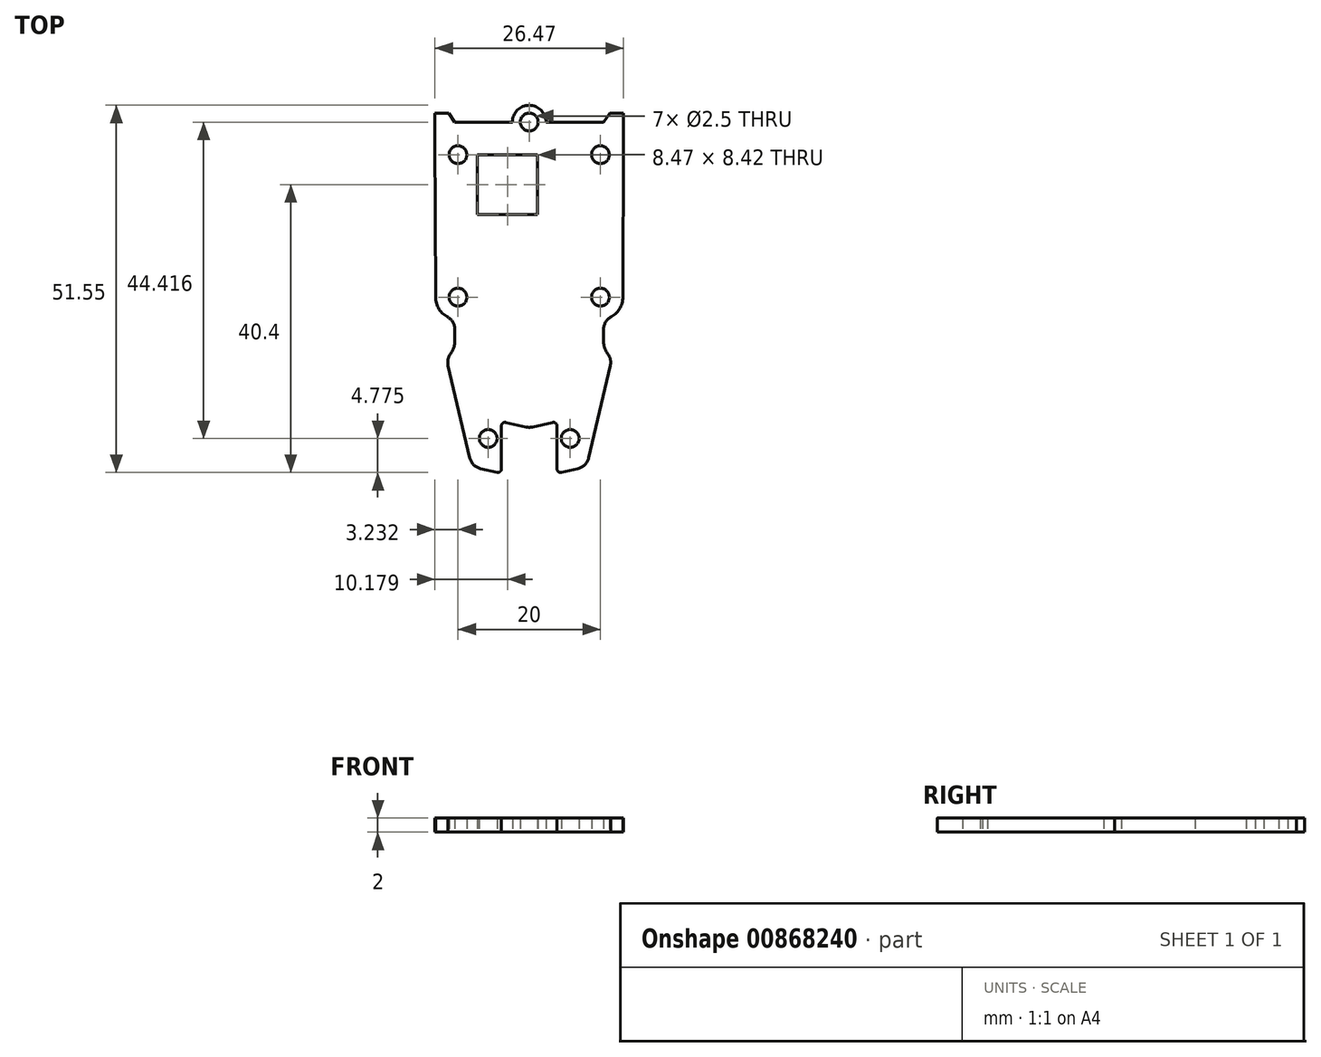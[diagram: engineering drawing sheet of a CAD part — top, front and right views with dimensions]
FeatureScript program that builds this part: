
annotation { "Feature Type Name" : "Feature", "Feature Type Description" : "" }
export const myFeature = defineFeature(function(context is Context, id is Id, definition is map)
    precondition{}
    {
        {
            var Q0;
            Q0=qCreatedBy(makeId("Top.planeOp"),FACE);
            var sketch = newSketch(context, id + "F0", { "sketchPlane" : qUnion([Q0])});
            skLineSegment(sketch, "E0.bottom", {"start": v(31.73, 23.79) * mm, "end": v(11.73, 23.79) * mm, "construction": true});
            skLineSegment(sketch, "E0.top", {"start": v(31.73, 43.79) * mm, "end": v(11.73, 43.79) * mm, "construction": true});
            skLineSegment(sketch, "E0.right", {"start": v(11.73, 23.79) * mm, "end": v(11.73, 43.79) * mm, "construction": true});
            skPoint(sketch, "E0.middle", {"position": v(21.73, 33.79) * mm});
            skCircle(sketch, "E1", {"center": v(11.73, 43.79) * mm, "radius": 1.25 * mm});
            skCircle(sketch, "E2.MirrorC", {"center": v(11.73, 23.79) * mm, "radius": 1.25 * mm});
            skLineSegment(sketch, "E3", {"start": v(12.51, 48.37) * mm, "end": v(19.38, 48.37) * mm});
            skLineSegment(sketch, "E4.MirrorCS", {"start": v(30.95, 48.37) * mm, "end": v(24.09, 48.37) * mm});
            skArc(sketch, "E5.0", {"start": v(10.25, 21.01) * mm, "mid": v(8.96, 22.28) * mm, "end": v(8.6, 24.05) * mm});
            skLineSegment(sketch, "E6", {"start": v(11.3, 17.66) * mm, "end": v(11.3, 19.25) * mm});
            skPoint(sketch, "E7.visualSharp", {"position": v(8.68, 24.79) * mm});
            skPoint(sketch, "E8.visualSharp", {"position": v(11.59, 20.92) * mm});
            skArc(sketch, "E8.filletArc", {"start": v(11.3, 19.25) * mm, "mid": v(11.02, 20.28) * mm, "end": v(10.25, 21.01) * mm});
            skPoint(sketch, "E9.orphan", {"position": v(11.3, 13.07) * mm});
            skArc(sketch, "E10.MirrorCS", {"start": v(33.8, 46.17) * mm, "mid": v(33.8, 46.16) * mm, "end": v(33.8, 46.16) * mm});
            skArc(sketch, "E11.MirrorCS", {"start": v(33.22, 21.01) * mm, "mid": v(34.5, 22.28) * mm, "end": v(34.87, 24.05) * mm});
            skArc(sketch, "E12.MirrorCS", {"start": v(32.16, 19.25) * mm, "mid": v(32.45, 20.28) * mm, "end": v(33.22, 21.01) * mm});
            skLineSegment(sketch, "E13.MirrorCS", {"start": v(32.16, 17.66) * mm, "end": v(32.16, 19.25) * mm});
            skCircle(sketch, "E14.MirrorC", {"center": v(31.73, 23.79) * mm, "radius": 1.25 * mm});
            skPoint(sketch, "E15.MirrorP", {"position": v(32.16, 20.67) * mm});
            skCircle(sketch, "E16.MirrorC", {"center": v(31.73, 43.79) * mm, "radius": 1.25 * mm});
            skPoint(sketch, "E17.MirrorP", {"position": v(32.16, 13.07) * mm});
            skLineSegment(sketch, "E18.MirrorCS", {"start": v(31.73, 23.79) * mm, "end": v(31.73, 43.79) * mm, "construction": true});
            skLineSegment(sketch, "E19", {"start": v(11.28, 48.36) * mm, "end": v(12.51, 48.37) * mm});
            skLineSegment(sketch, "E20.MirrorCS", {"start": v(32.18, 48.36) * mm, "end": v(30.95, 48.37) * mm});
            skPoint(sketch, "E21.MirrorCS.end.orphan", {"position": v(30.95, 48.37) * mm});
            skArc(sketch, "E22", {"start": v(24.09, 48.37) * mm, "mid": v(21.73, 50.73) * mm, "end": v(19.38, 48.37) * mm});
            skCircle(sketch, "E23", {"center": v(21.73, 48.37) * mm, "radius": 1.25 * mm});
            skCircle(sketch, "E24", {"center": v(15.98, 3.96) * mm, "radius": 1.25 * mm});
            skCircle(sketch, "E25.MirrorC", {"center": v(27.48, 3.96) * mm, "radius": 1.25 * mm});
            skPoint(sketch, "E26.visualSharp", {"position": v(11.3, 16.16) * mm});
            skArc(sketch, "E26.filletArc", {"start": v(10.7, 15.85) * mm, "mid": v(11.15, 16.7) * mm, "end": v(11.3, 17.66) * mm});
            skPoint(sketch, "E27.visualSharp", {"position": v(32.16, 16.16) * mm});
            skArc(sketch, "E27.filletArc", {"start": v(32.16, 17.66) * mm, "mid": v(32.32, 16.7) * mm, "end": v(32.76, 15.85) * mm});
            skPoint(sketch, "E28.MirrorP", {"position": v(33.1, 46.2) * mm});
            skPoint(sketch, "E29.visualSharp", {"position": v(29.24, 0.28) * mm});
            skLineSegment(sketch, "E30.MirrorCS", {"start": v(28.57, -0.28) * mm, "end": v(26.24, -0.8) * mm});
            skLineSegment(sketch, "E31", {"start": v(10.35, 14.2) * mm, "end": v(13.39, 1.22) * mm});
            skLineSegment(sketch, "E32", {"start": v(33.11, 14.2) * mm, "end": v(30.08, 1.22) * mm});
            skLineSegment(sketch, "E33", {"start": v(17.83, -0.32) * mm, "end": v(17.83, 5.72) * mm});
            skLineSegment(sketch, "E34", {"start": v(18.45, 6.2) * mm, "end": v(21.29, 5.56) * mm});
            skLineSegment(sketch, "E35", {"start": v(21.73, 5.46) * mm, "end": v(21.73, -1.74) * mm, "construction": true});
            skLineSegment(sketch, "E36.MirrorCS", {"start": v(25.02, 6.2) * mm, "end": v(22.17, 5.56) * mm});
            skLineSegment(sketch, "E37.MirrorCS", {"start": v(25.63, -0.32) * mm, "end": v(25.63, 5.72) * mm});
            skPoint(sketch, "E38.center.orphan", {"position": v(21.73, 3.42) * mm});
            skPoint(sketch, "E39.visualSharp", {"position": v(13.67, 0) * mm});
            skPoint(sketch, "E40.visualSharp", {"position": v(29.8, 0) * mm});
            skArc(sketch, "E40.filletArc", {"start": v(28.57, -0.28) * mm, "mid": v(29.54, 0.25) * mm, "end": v(30.08, 1.22) * mm});
            skLineSegment(sketch, "E41.MirrorCS", {"start": v(14.9, -0.28) * mm, "end": v(17.22, -0.8) * mm});
            skArc(sketch, "E42.MirrorCS", {"start": v(14.9, -0.28) * mm, "mid": v(13.93, 0.25) * mm, "end": v(13.39, 1.22) * mm});
            skPoint(sketch, "E43.visualSharp", {"position": v(17.83, -0.94) * mm});
            skArc(sketch, "E43.filletArc", {"start": v(17.22, -0.8) * mm, "mid": v(17.65, -0.7) * mm, "end": v(17.83, -0.32) * mm});
            skPoint(sketch, "E44.visualSharp", {"position": v(25.63, -0.94) * mm});
            skArc(sketch, "E44.filletArc", {"start": v(25.63, -0.32) * mm, "mid": v(25.82, -0.7) * mm, "end": v(26.24, -0.8) * mm});
            skPoint(sketch, "E45.visualSharp", {"position": v(25.63, 6.34) * mm});
            skArc(sketch, "E45.filletArc", {"start": v(25.63, 5.72) * mm, "mid": v(25.44, 6.1) * mm, "end": v(25.02, 6.2) * mm});
            skPoint(sketch, "E46.visualSharp", {"position": v(17.83, 6.34) * mm});
            skArc(sketch, "E46.filletArc", {"start": v(18.45, 6.2) * mm, "mid": v(18.02, 6.1) * mm, "end": v(17.83, 5.72) * mm});
            skPoint(sketch, "E47.visualSharp", {"position": v(21.73, 5.46) * mm});
            skArc(sketch, "E47.filletArc", {"start": v(21.29, 5.56) * mm, "mid": v(21.73, 5.5) * mm, "end": v(22.17, 5.56) * mm});
            skPoint(sketch, "E48.visualSharp", {"position": v(33.36, 15.26) * mm});
            skArc(sketch, "E48.filletArc", {"start": v(33.11, 14.2) * mm, "mid": v(33.12, 15.06) * mm, "end": v(32.76, 15.85) * mm});
            skPoint(sketch, "E49.visualSharp", {"position": v(10.1, 15.26) * mm});
            skArc(sketch, "E49.filletArc", {"start": v(10.7, 15.85) * mm, "mid": v(10.34, 15.06) * mm, "end": v(10.35, 14.2) * mm});
            skLineSegment(sketch, "E50", {"start": v(8.6, 24.05) * mm, "end": v(8.5, 46.11) * mm});
            skLineSegment(sketch, "E51", {"start": v(8.5, 46.11) * mm, "end": v(8.5, 49.62) * mm});
            skLineSegment(sketch, "E52", {"start": v(8.5, 49.62) * mm, "end": v(10.42, 49.62) * mm});
            skLineSegment(sketch, "E53", {"start": v(10.42, 49.62) * mm, "end": v(11.28, 48.36) * mm});
            skLineSegment(sketch, "E54", {"start": v(21.73, 48.37) * mm, "end": v(21.73, 44.84) * mm, "construction": true});
            skLineSegment(sketch, "E55.MirrorCS", {"start": v(33.04, 49.62) * mm, "end": v(32.18, 48.36) * mm});
            skLineSegment(sketch, "E56.MirrorCS", {"start": v(34.97, 49.62) * mm, "end": v(33.04, 49.62) * mm});
            skLineSegment(sketch, "E57.MirrorCS", {"start": v(34.97, 46.11) * mm, "end": v(34.97, 49.62) * mm});
            skLineSegment(sketch, "E58.MirrorCS", {"start": v(34.87, 24.05) * mm, "end": v(34.97, 46.11) * mm});
            skLineSegment(sketch, "E59.bottom", {"start": v(14.45, 43.79) * mm, "end": v(22.91, 43.79) * mm});
            skLineSegment(sketch, "E59.top", {"start": v(14.45, 35.37) * mm, "end": v(22.91, 35.37) * mm});
            skLineSegment(sketch, "E59.left", {"start": v(14.45, 43.79) * mm, "end": v(14.45, 35.37) * mm});
            skLineSegment(sketch, "E59.right", {"start": v(22.91, 43.79) * mm, "end": v(22.91, 35.37) * mm});
            skSolve(sketch);
        }
        {
            var Q0;
            Q0 = qSketchRegion(id + "F0", true);
            extrude(context, id + "F1", {"entities" : qUnion([Q0]), "depth" : 2 * mm, "offsetDistance" : 25 * mm});
        }
    });
